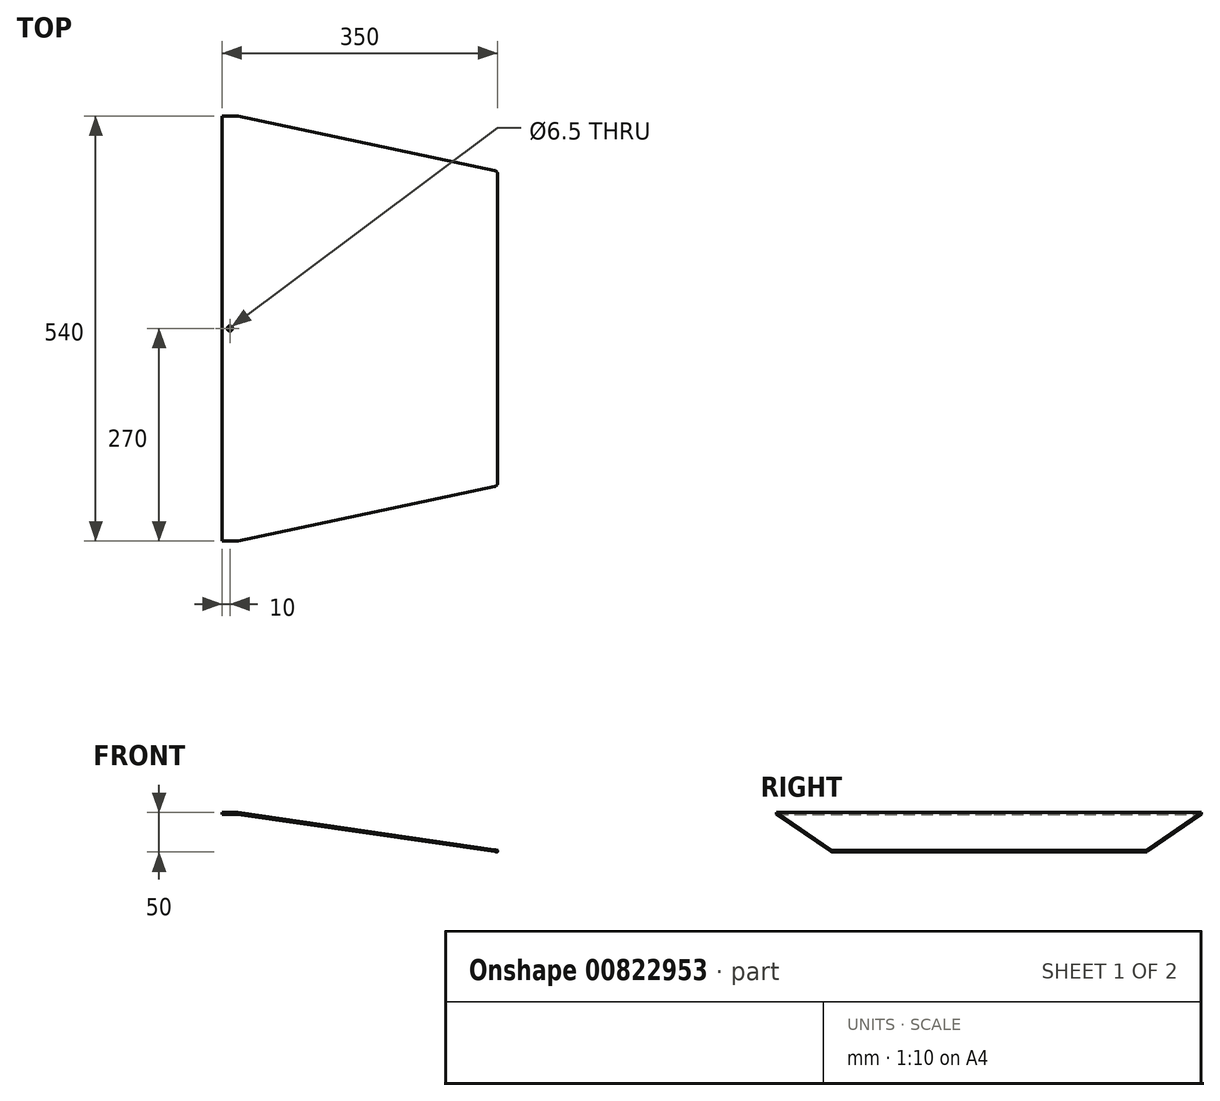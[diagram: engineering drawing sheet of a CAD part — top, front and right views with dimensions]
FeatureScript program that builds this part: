
annotation { "Feature Type Name" : "Feature", "Feature Type Description" : "" }
export const myFeature = defineFeature(function(context is Context, id is Id, definition is map)
    precondition{}
    {
        {
            var Q0;
            Q0=qCreatedBy(makeId("Front.planeOp"),FACE);
            var sketch = newSketch(context, id + "F0", { "sketchPlane" : qUnion([Q0])});
            skLineSegment(sketch, "E0", {"start": v(0, 0) * mm, "end": v(20, 0) * mm});
            skLineSegment(sketch, "E1", {"start": v(20, 0) * mm, "end": v(350, -48.02) * mm});
            skLineSegment(sketch, "E2.0", {"start": v(19.86, -2) * mm, "end": v(349.71, -50) * mm});
            skLineSegment(sketch, "E2.1", {"start": v(0, -2) * mm, "end": v(19.86, -2) * mm});
            skLineSegment(sketch, "E3", {"start": v(349.71, -50) * mm, "end": v(350, -48.02) * mm});
            skLineSegment(sketch, "E4", {"start": v(0, 0) * mm, "end": v(0, -2) * mm});
            skSolve(sketch);
        }
        {
            var Q0;
            Q0 = qSketchRegion(id + "F0", true);
            extrude(context, id + "F1", {"entities" : qUnion([Q0]), "endBound" : BoundingType.SYMMETRIC, "depth" : 540 * mm, "offsetDistance" : 25 * mm});
        }
        {
            var Q0;
            Q0=makeQuery(id+"F1.opExtrude","SWEPT_FACE",FACE,{"disambiguationData":[OSD([sQuery(id+"F0.wireOp",EDGE,"E0")])]});
            var sketch = newSketch(context, id + "F2", { "sketchPlane" : qUnion([Q0])});
            skLineSegment(sketch, "E5.0", {"start": v(0, -270) * mm, "end": v(0, 270) * mm, "construction": true});
            skLineSegment(sketch, "E6.0", {"start": v(0, 270) * mm, "end": v(20, 270) * mm, "construction": true});
            skLineSegment(sketch, "E7.0", {"start": v(0, -270) * mm, "end": v(20, -270) * mm, "construction": true});
            skLineSegment(sketch, "E8", {"start": v(20, -270) * mm, "end": v(350, -200) * mm});
            skLineSegment(sketch, "E9", {"start": v(0, 0) * mm, "end": v(333.61, 0) * mm, "construction": true});
            skLineSegment(sketch, "E10.0", {"start": v(350, -270) * mm, "end": v(350, 270) * mm, "construction": true});
            skLineSegment(sketch, "E11.MirrorCS", {"start": v(20, 270) * mm, "end": v(350, 200) * mm});
            skLineSegment(sketch, "E12", {"start": v(20, -270) * mm, "end": v(20, -308.05) * mm});
            skLineSegment(sketch, "E13", {"start": v(20, -308.05) * mm, "end": v(437.2, -308.05) * mm});
            skLineSegment(sketch, "E14", {"start": v(437.2, -308.05) * mm, "end": v(437.2, -200) * mm});
            skLineSegment(sketch, "E15", {"start": v(437.2, -200) * mm, "end": v(350, -200) * mm});
            skLineSegment(sketch, "E16.MirrorCS", {"start": v(437.2, 200) * mm, "end": v(350, 200) * mm});
            skLineSegment(sketch, "E17.MirrorCS", {"start": v(437.2, 308.05) * mm, "end": v(437.2, 200) * mm});
            skLineSegment(sketch, "E18.MirrorCS", {"start": v(20, 308.05) * mm, "end": v(437.2, 308.05) * mm});
            skLineSegment(sketch, "E19.MirrorCS", {"start": v(20, 270) * mm, "end": v(20, 308.05) * mm});
            skLineSegment(sketch, "E20", {"start": v(0, 270) * mm, "end": v(20, 308.05) * mm, "construction": true});
            skLineSegment(sketch, "E21", {"start": v(0, 270) * mm, "end": v(350, 200) * mm, "construction": true});
            skLineSegment(sketch, "E22", {"start": v(0, -270) * mm, "end": v(20, -308.05) * mm, "construction": true});
            skLineSegment(sketch, "E23", {"start": v(0, -270) * mm, "end": v(350, -200) * mm, "construction": true});
            skSolve(sketch);
        }
        {
            var Q0;
            Q0 = qSketchRegion(id + "F2", true);
            extrude(context, id + "F3", {"entities" : qUnion([Q0]), "operationType" : NewBodyOperationType.REMOVE, "oppositeDirection" : true, "depth" : 55 * mm, "offsetDistance" : 25 * mm});
        }
        {
            var Q0;
            Q0=makeQuery(id+"F1.opExtrude","SWEPT_EDGE",EDGE,{"disambiguationData":[OSD([sQuery(id+"F0.wireOp",EDGE,"E0"),sQuery(id+"F0.wireOp",EDGE,"E1")])]});
            fillet(context, id + "F4", {"entities" : qUnion([Q0]), "radius" : 4 * mm, "tangentPropagation" : true, "allowEdgeOverflow" : false});
        }
        {
            var Q0;
            Q0=makeQuery(id+"F1.opExtrude","SWEPT_EDGE",EDGE,{"disambiguationData":[OSD([sQuery(id+"F0.wireOp",EDGE,"E2.0"),sQuery(id+"F0.wireOp",EDGE,"E2.1")])]});
            fillet(context, id + "F5", {"entities" : qUnion([Q0]), "radius" : 2 * mm, "tangentPropagation" : true, "allowEdgeOverflow" : false});
        }
        {
            var Q0;
            Q0=makeQuery(id+"F3.boolean.opBoolean","INTERSECT",EDGE,{"derivedFrom":[makeQuery(id+"F1.opExtrude","SWEPT_FACE",FACE,{"disambiguationData":[OSD([sQuery(id+"F0.wireOp",EDGE,"E3")])]}),makeQuery(id+"F3.opExtrude","SWEPT_FACE",FACE,{"disambiguationData":[OSD([sQuery(id+"F2.wireOp",EDGE,"E8")])]})]});
            var Q1;
            Q1=makeQuery(id+"F3.boolean.opBoolean","INTERSECT",EDGE,{"derivedFrom":[makeQuery(id+"F1.opExtrude","SWEPT_FACE",FACE,{"disambiguationData":[OSD([sQuery(id+"F0.wireOp",EDGE,"E3")])]}),makeQuery(id+"F3.opExtrude","SWEPT_FACE",FACE,{"disambiguationData":[OSD([sQuery(id+"F2.wireOp",EDGE,"E11.MirrorCS")])]})]});
            fillet(context, id + "F6", {"entities" : qUnion([Q0, Q1]), "radius" : 5 * mm, "tangentPropagation" : true, "allowEdgeOverflow" : false});
        }
        {
            var Q0;
            Q0=makeQuery(id+"F1.opExtrude","SWEPT_FACE",FACE,{"disambiguationData":[OSD([sQuery(id+"F0.wireOp",EDGE,"E0")])]});
            var sketch = newSketch(context, id + "F7", { "sketchPlane" : qUnion([Q0])});
            skLineSegment(sketch, "E24", {"start": v(0, 0) * mm, "end": v(10, 0) * mm, "construction": true});
            skCircle(sketch, "E25", {"center": v(10, 0) * mm, "radius": 3.25 * mm});
            skSolve(sketch);
        }
        {
            var Q0;
            Q0 = qSketchRegion(id + "F7", true);
            extrude(context, id + "F8", {"entities" : qUnion([Q0]), "operationType" : NewBodyOperationType.REMOVE, "oppositeDirection" : true, "depth" : 25 * mm, "offsetDistance" : 25 * mm});
        }
    });
